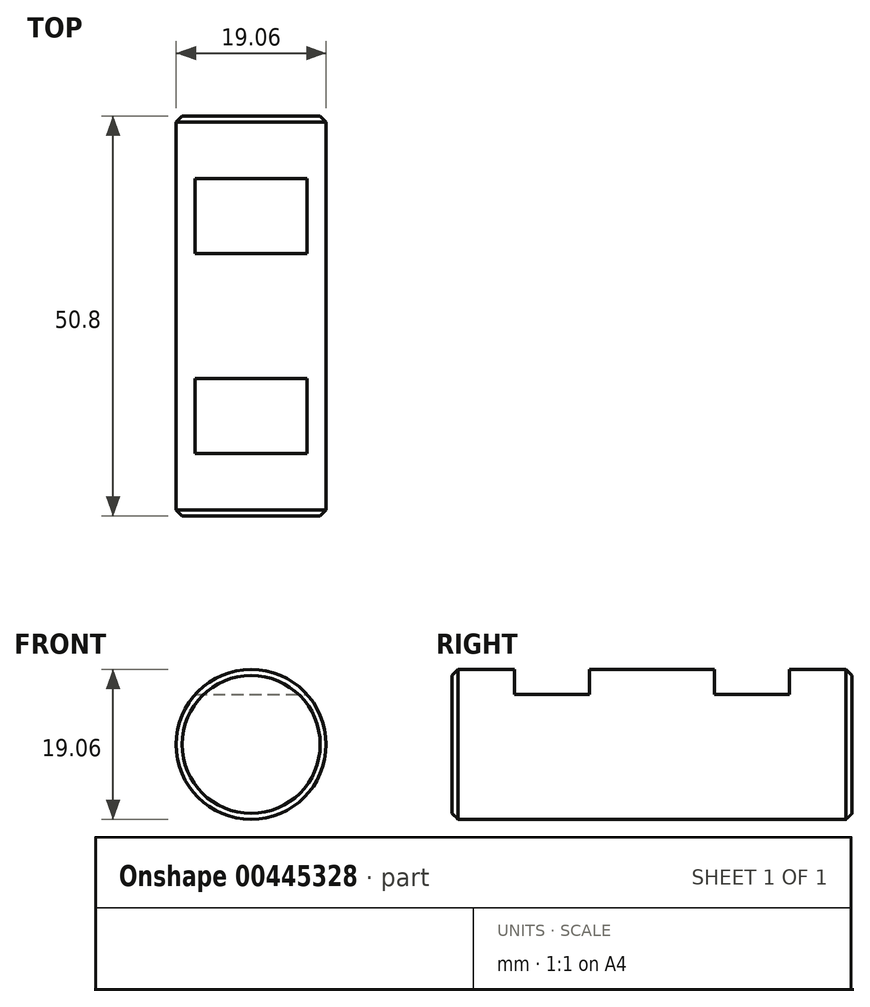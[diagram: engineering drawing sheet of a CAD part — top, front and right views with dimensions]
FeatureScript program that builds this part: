
annotation { "Feature Type Name" : "Feature", "Feature Type Description" : "" }
export const myFeature = defineFeature(function(context is Context, id is Id, definition is map)
    precondition{}
    {
        {
            var Q0;
            Q0=qCreatedBy(makeId("Front.planeOp"),FACE);
            var sketch = newSketch(context, id + "F0", { "sketchPlane" : qUnion([Q0])});
            skCircle(sketch, "E0", {"center": v(0, 0) * mm, "radius": 9.53 * mm});
            skSolve(sketch);
        }
        {
            var Q0;
            Q0=makeQuery(id+"F0.imprint","IMPRINT",FACE,{"disambiguationData":[TD([[makeQuery(id+"F0.imprint","IMPRINT",EDGE,{"derivedFrom":sQuery(id+"F0.wireOp",EDGE,"E0")}),1.0]])]});
            extrude(context, id + "F1", {"entities" : qUnion([Q0]), "oppositeDirection" : true, "depth" : 50.8 * mm});
        }
        {
            var Q0;
            Q0=makeQuery(id+"F1.opExtrude","CAP_EDGE",EDGE,{"disambiguationData":[OSD([sQuery(id+"F0.wireOp",EDGE,"E0")])],"isStart":true});
            var Q1;
            Q1=makeQuery(id+"F1.opExtrude","CAP_EDGE",EDGE,{"disambiguationData":[OSD([sQuery(id+"F0.wireOp",EDGE,"E0")])],"isStart":false});
            chamfer(context, id + "F2", {"entities" : qUnion([Q0, Q1]), "width" : 0.76 * mm, "tangentPropagation" : true});
        }
        {
            var Q0;
            Q0=qCreatedBy(makeId("Right.planeOp"),FACE);
            var sketch = newSketch(context, id + "F3", { "sketchPlane" : qUnion([Q0])});
            skLineSegment(sketch, "E1", {"start": v(0, 0) * mm, "end": v(0, 20.13) * mm, "construction": true});
            skLineSegment(sketch, "E2.0", {"start": v(25.4, 0) * mm, "end": v(25.4, 20.13) * mm, "construction": true});
            skLineSegment(sketch, "E3.0", {"start": v(38.1, 0) * mm, "end": v(38.1, 20.13) * mm, "construction": true});
            skLineSegment(sketch, "E4.0", {"start": v(12.7, 0) * mm, "end": v(12.7, 20.13) * mm, "construction": true});
            skLineSegment(sketch, "E5.0", {"start": v(17.46, 6.35) * mm, "end": v(17.46, 12.1) * mm});
            skLineSegment(sketch, "E6.0", {"start": v(7.94, 6.35) * mm, "end": v(7.94, 12.1) * mm});
            skLineSegment(sketch, "E7.0", {"start": v(42.86, 6.35) * mm, "end": v(42.86, 12.1) * mm});
            skLineSegment(sketch, "E8.0", {"start": v(33.34, 6.35) * mm, "end": v(33.34, 12.1) * mm});
            skLineSegment(sketch, "E9", {"start": v(0, 0) * mm, "end": v(61.33, 0) * mm, "construction": true});
            skLineSegment(sketch, "E10.0", {"start": v(7.94, 6.35) * mm, "end": v(17.46, 6.35) * mm});
            skLineSegment(sketch, "E11", {"start": v(7.94, 12.1) * mm, "end": v(17.46, 12.1) * mm});
            skLineSegment(sketch, "E12.trimOffspring", {"start": v(33.34, 12.1) * mm, "end": v(42.86, 12.1) * mm});
            skLineSegment(sketch, "E13.trimOffspring", {"start": v(33.34, 6.35) * mm, "end": v(42.86, 6.35) * mm});
            skSolve(sketch);
        }
        {
            var Q0;
            Q0=makeQuery(id+"F3.imprint","IMPRINT",FACE,{"disambiguationData":[TD([[makeQuery(id+"F3.imprint","IMPRINT",EDGE,{"derivedFrom":sQuery(id+"F3.wireOp",EDGE,"E5.0")}),1.0]])]});
            var Q1;
            Q1=makeQuery(id+"F3.imprint","IMPRINT",FACE,{"disambiguationData":[TD([[makeQuery(id+"F3.imprint","IMPRINT",EDGE,{"derivedFrom":sQuery(id+"F3.wireOp",EDGE,"E7.0")}),1.0]])]});
            var Q2;
            Q2=sQuery(id+"F3.wireOp",EDGE,"E1");
            var Q3;
            Q3=sQuery(id+"F3.wireOp",EDGE,"E9");
            var Q4;
            Q4=sQuery(id+"F3.wireOp",EDGE,"E4.0");
            var Q5;
            Q5=sQuery(id+"F3.wireOp",EDGE,"E2.0");
            var Q6;
            Q6=sQuery(id+"F3.wireOp",EDGE,"E3.0");
            var Q7;
            Q7=sQuery(id+"F3.wireOp",EDGE,"E11");
            var Q8;
            Q8=sQuery(id+"F3.wireOp",EDGE,"E6.0");
            var Q9;
            Q9=sQuery(id+"F3.wireOp",EDGE,"E10.0");
            var Q10;
            Q10=sQuery(id+"F3.wireOp",EDGE,"E5.0");
            extrude(context, id + "F4", {"entities" : qUnion([Q0, Q1]), "operationType" : NewBodyOperationType.REMOVE, "surfaceEntities" : qUnion([Q2, Q3, Q4, Q5, Q6, Q7, Q8, Q9, Q10]), "endBound" : BoundingType.SYMMETRIC, "oppositeDirection" : true, "depth" : 25.4 * mm});
        }
    });
